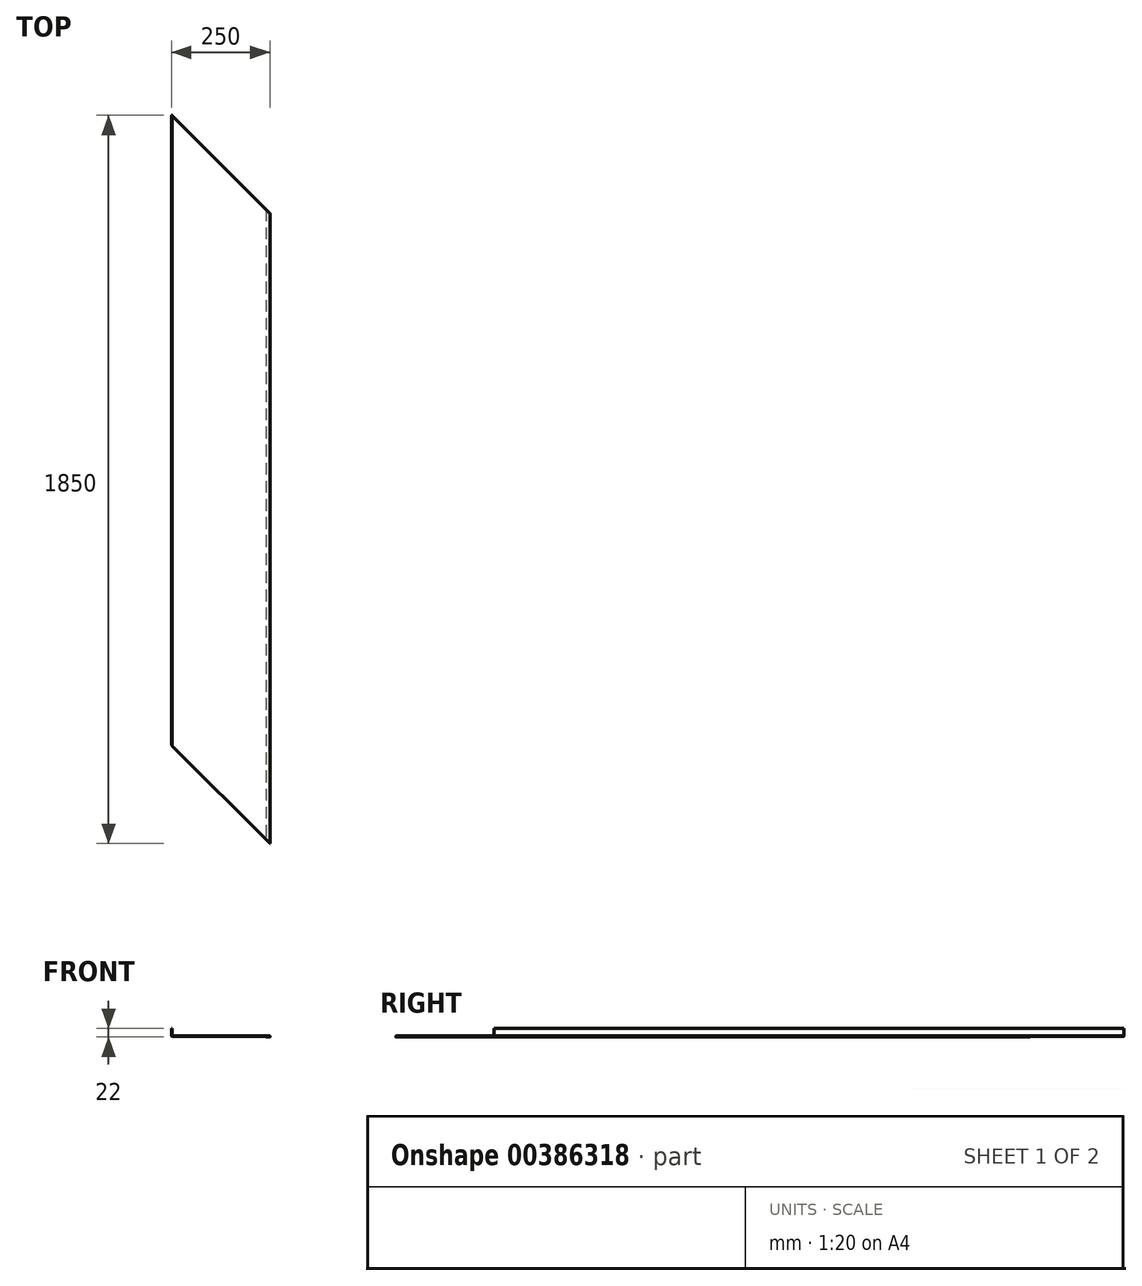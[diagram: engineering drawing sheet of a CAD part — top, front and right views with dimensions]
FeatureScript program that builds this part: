
annotation { "Feature Type Name" : "Feature", "Feature Type Description" : "" }
export const myFeature = defineFeature(function(context is Context, id is Id, definition is map)
    precondition{}
    {
        {
            var Q0;
            Q0=qCreatedBy(makeId("Front.planeOp"),FACE);
            var sketch = newSketch(context, id + "F0", { "sketchPlane" : qUnion([Q0])});
            skLineSegment(sketch, "E0", {"start": v(0, 19) * mm, "end": v(0, 1) * mm});
            skLineSegment(sketch, "E1", {"start": v(1, 0) * mm, "end": v(248, 0) * mm});
            skLineSegment(sketch, "E2", {"start": v(0, 19) * mm, "end": v(-1, 19) * mm});
            skLineSegment(sketch, "E3", {"start": v(-1, 19) * mm, "end": v(-1, 1) * mm});
            skLineSegment(sketch, "E4", {"start": v(1, -1) * mm, "end": v(248, -1) * mm});
            skLineSegment(sketch, "E5", {"start": v(249, 0) * mm, "end": v(249, 0) * mm});
            skPoint(sketch, "E6.visualSharp", {"position": v(-1, -1) * mm});
            skArc(sketch, "E6.filletArc", {"start": v(-1, 1) * mm, "mid": v(-0.41, -0.41) * mm, "end": v(1, -1) * mm});
            skPoint(sketch, "E7.visualSharp", {"position": v(0, 0) * mm});
            skArc(sketch, "E7.filletArc", {"start": v(0, 1) * mm, "mid": v(0.3, 0.3) * mm, "end": v(1, 0) * mm});
            skPoint(sketch, "E8.visualSharp", {"position": v(246.55, 1.97) * mm});
            skPoint(sketch, "E9.visualSharp", {"position": v(249, -1) * mm});
            skLineSegment(sketch, "E10", {"start": v(239, -2) * mm, "end": v(239, -3) * mm});
            skLineSegment(sketch, "E11", {"start": v(239, -3) * mm, "end": v(248, -3) * mm});
            skLineSegment(sketch, "E12", {"start": v(239, -2) * mm, "end": v(248, -2) * mm});
            skLineSegment(sketch, "E13", {"start": v(248, -1) * mm, "end": v(248, -2) * mm});
            skLineSegment(sketch, "E14", {"start": v(249, -1) * mm, "end": v(249, -2) * mm});
            skPoint(sketch, "E15.visualSharp", {"position": v(249, -3) * mm});
            skArc(sketch, "E15.filletArc", {"start": v(248, -3) * mm, "mid": v(248.7, -2.7) * mm, "end": v(249, -2) * mm});
            skPoint(sketch, "E16.visualSharp", {"position": v(249, 0) * mm});
            skArc(sketch, "E16.filletArc", {"start": v(249, -1) * mm, "mid": v(248.7, -0.3) * mm, "end": v(248, 0) * mm});
            skSolve(sketch);
        }
        {
            var Q0;
            Q0 = qSketchRegion(id + "F0", true);
            var Q1;
            Q1 = qConstructionFilter(qBodyType(qCreatedBy(id + "F0" ,EDGE), BodyType.WIRE), ConstructionObject.NO);
            extrude(context, id + "F1", {"entities" : qUnion([Q0]), "surfaceEntities" : qUnion([Q1]), "oppositeDirection" : true, "depth" : 1850 * mm});
        }
        {
            var Q0;
            Q0=makeQuery(id+"F1.opExtrude","SWEPT_FACE",FACE,{"disambiguationData":[OSD([sQuery(id+"F0.wireOp",EDGE,"E1")])]});
            var sketch = newSketch(context, id + "F2", { "sketchPlane" : qUnion([Q0])});
            skLineSegment(sketch, "E17", {"start": v(249, 0) * mm, "end": v(-151, 400) * mm});
            skLineSegment(sketch, "E18", {"start": v(-151, 0) * mm, "end": v(249, 0) * mm, "construction": true});
            skLineSegment(sketch, "E19", {"start": v(-151, 0) * mm, "end": v(-151, 400) * mm});
            skLineSegment(sketch, "E20", {"start": v(249, 0) * mm, "end": v(249, -77.8) * mm});
            skLineSegment(sketch, "E21", {"start": v(249, -77.8) * mm, "end": v(-141.14, -77.8) * mm});
            skLineSegment(sketch, "E22", {"start": v(-141.14, -77.8) * mm, "end": v(-151, 0) * mm});
            skSolve(sketch);
        }
        {
            var Q0;
            Q0 = qSketchRegion(id + "F2", true);
            extrude(context, id + "F3", {"entities" : qUnion([Q0]), "operationType" : NewBodyOperationType.REMOVE, "endBound" : BoundingType.SYMMETRIC, "oppositeDirection" : true, "depth" : 50 * mm, "hasSecondDirection" : true, "secondDirectionOppositeDirection" : true, "secondDirectionDepth" : 50 * mm});
        }
        {
            var Q0;
            Q0=makeQuery(id+"F1.opExtrude","SWEPT_FACE",FACE,{"disambiguationData":[OSD([sQuery(id+"F0.wireOp",EDGE,"E1")])]});
            var sketch = newSketch(context, id + "F4", { "sketchPlane" : qUnion([Q0])});
            skLineSegment(sketch, "E23", {"start": v(0, 1850) * mm, "end": v(456.1, 1393.9) * mm});
            skLineSegment(sketch, "E24", {"start": v(456.1, 1393.9) * mm, "end": v(456.1, 1893.9) * mm});
            skLineSegment(sketch, "E25", {"start": v(456.1, 1893.9) * mm, "end": v(0, 1893.9) * mm});
            skLineSegment(sketch, "E26", {"start": v(0, 1893.9) * mm, "end": v(0, 1850) * mm});
            skSolve(sketch);
        }
        {
            var Q0;
            Q0 = qSketchRegion(id + "F4", true);
            extrude(context, id + "F5", {"entities" : qUnion([Q0]), "operationType" : NewBodyOperationType.REMOVE, "endBound" : BoundingType.SYMMETRIC, "oppositeDirection" : true, "depth" : 50 * mm});
        }
    });
